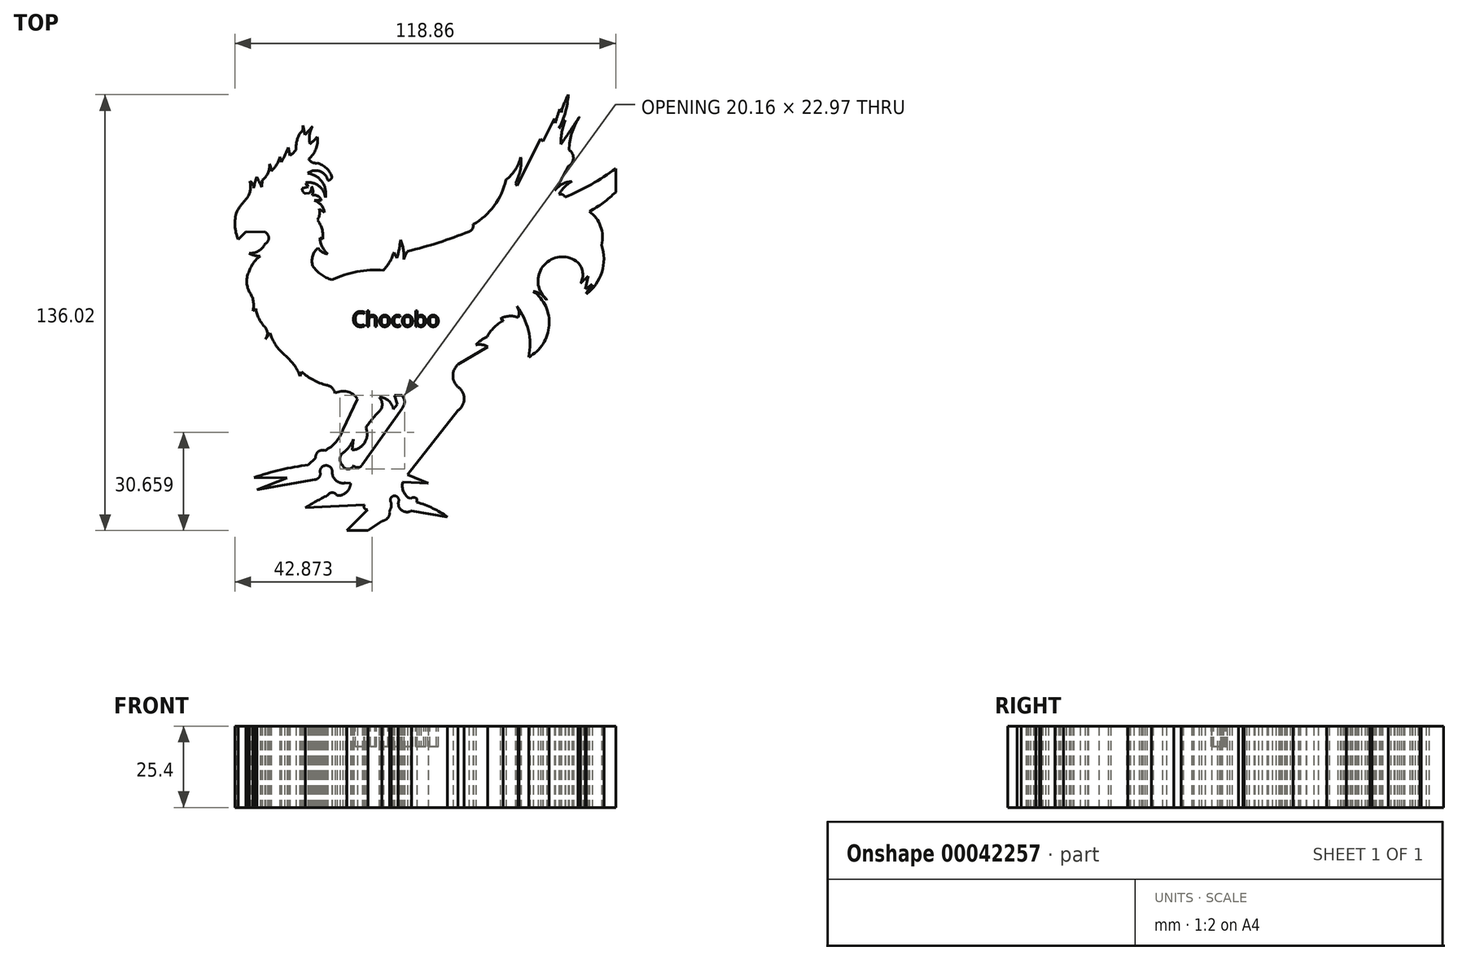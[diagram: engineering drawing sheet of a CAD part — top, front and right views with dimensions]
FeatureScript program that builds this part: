
annotation { "Feature Type Name" : "Feature", "Feature Type Description" : "" }
export const myFeature = defineFeature(function(context is Context, id is Id, definition is map)
    precondition{}
    {
        {
            var Q0;
            Q0=qCreatedBy(makeId("Top.planeOp"),FACE);
            var sketch = newSketch(context, id + "F0", { "sketchPlane" : qUnion([Q0])});
            skPoint(sketch, "E0", {"position": v(0, 127) * mm});
            skPoint(sketch, "E1", {"position": v(43.07, 0) * mm});
            skPoint(sketch, "E2", {"position": v(49.64, 0) * mm});
            skPoint(sketch, "E3", {"position": v(74.47, 4.17) * mm});
            skPoint(sketch, "E4", {"position": v(30.16, 7.09) * mm});
            skPoint(sketch, "E5", {"position": v(53.96, 2.95) * mm});
            skArc(sketch, "E6", {"start": v(48.55, 7.99) * mm, "mid": v(48.58, 6.94) * mm, "end": v(49.55, 6.53) * mm});
            skLineSegment(sketch, "E7", {"start": v(49.55, 6.53) * mm, "end": v(43.07, 0) * mm});
            skLineSegment(sketch, "E8", {"start": v(43.07, 0) * mm, "end": v(49.64, 0) * mm});
            skLineSegment(sketch, "E9", {"start": v(49.64, 0) * mm, "end": v(53.96, 2.95) * mm});
            skLineSegment(sketch, "E10", {"start": v(30.16, 7.09) * mm, "end": v(48.55, 7.99) * mm});
            skPoint(sketch, "E11", {"position": v(37.05, 10.94) * mm});
            skArc(sketch, "E12", {"start": v(37.05, 10.94) * mm, "mid": v(33.53, 9.15) * mm, "end": v(30.16, 7.09) * mm});
            skArc(sketch, "E13", {"start": v(40, 10.94) * mm, "mid": v(38.52, 11.85) * mm, "end": v(37.05, 10.94) * mm});
            skArc(sketch, "E14", {"start": v(40, 10.94) * mm, "mid": v(42.95, 11.93) * mm, "end": v(44.25, 14.75) * mm});
            skArc(sketch, "E15", {"start": v(53.96, 2.95) * mm, "mid": v(55.9, 4.03) * mm, "end": v(56.46, 6.17) * mm});
            skArc(sketch, "E16", {"start": v(59.19, 8.98) * mm, "mid": v(57.8, 10.82) * mm, "end": v(56.93, 8.68) * mm});
            skArc(sketch, "E17", {"start": v(56.46, 6.17) * mm, "mid": v(56.91, 7.39) * mm, "end": v(56.93, 8.68) * mm});
            skArc(sketch, "E18", {"start": v(59.19, 8.98) * mm, "mid": v(60.32, 6.26) * mm, "end": v(63.26, 6.17) * mm});
            skLineSegment(sketch, "E19", {"start": v(63.26, 6.17) * mm, "end": v(74.47, 4.17) * mm});
            skPoint(sketch, "E20", {"position": v(64.97, 8.83) * mm});
            skPoint(sketch, "E21", {"position": v(64.97, 9.94) * mm});
            skPoint(sketch, "E22", {"position": v(62.86, 9.94) * mm});
            skArc(sketch, "E23", {"start": v(74.47, 4.17) * mm, "mid": v(69.94, 6.95) * mm, "end": v(64.97, 8.83) * mm});
            skLineSegment(sketch, "E24", {"start": v(64.97, 8.83) * mm, "end": v(64.97, 9.94) * mm});
            skArc(sketch, "E25", {"start": v(64.97, 9.94) * mm, "mid": v(63.91, 10.34) * mm, "end": v(62.86, 9.94) * mm});
            skArc(sketch, "E26", {"start": v(60.55, 15.16) * mm, "mid": v(60.78, 12.14) * mm, "end": v(62.86, 9.94) * mm});
            skArc(sketch, "E27", {"start": v(38.52, 18.21) * mm, "mid": v(36.65, 20.32) * mm, "end": v(34.7, 18.3) * mm});
            skArc(sketch, "E28", {"start": v(38.52, 18.21) * mm, "mid": v(39.76, 15.56) * mm, "end": v(42.61, 14.87) * mm});
            skLineSegment(sketch, "E29", {"start": v(42.61, 14.87) * mm, "end": v(44.25, 14.75) * mm});
            skPoint(sketch, "E30", {"position": v(33.07, 15.89) * mm});
            skPoint(sketch, "E31", {"position": v(24.37, 16.42) * mm});
            skPoint(sketch, "E32", {"position": v(14.07, 16.56) * mm});
            skPoint(sketch, "E33", {"position": v(15.04, 12.74) * mm});
            skPoint(sketch, "E34", {"position": v(31.04, 20.48) * mm});
            skArc(sketch, "E35", {"start": v(33.07, 15.89) * mm, "mid": v(34.49, 16.68) * mm, "end": v(34.7, 18.3) * mm});
            skLineSegment(sketch, "E36", {"start": v(15.04, 12.74) * mm, "end": v(33.07, 15.89) * mm});
            skLineSegment(sketch, "E37", {"start": v(24.37, 16.42) * mm, "end": v(15.04, 12.74) * mm});
            skLineSegment(sketch, "E38", {"start": v(24.37, 16.42) * mm, "end": v(14.07, 16.56) * mm});
            skArc(sketch, "E39", {"start": v(31.04, 20.48) * mm, "mid": v(22.46, 18.95) * mm, "end": v(14.07, 16.56) * mm});
            skPoint(sketch, "E40", {"position": v(68.53, 14.79) * mm});
            skPoint(sketch, "E41", {"position": v(61.96, 17.38) * mm});
            skLineSegment(sketch, "E42", {"start": v(60.55, 15.16) * mm, "end": v(68.53, 14.79) * mm});
            skLineSegment(sketch, "E43", {"start": v(61.96, 17.38) * mm, "end": v(68.53, 14.79) * mm});
            skPoint(sketch, "E44", {"position": v(77.8, 37.53) * mm});
            skPoint(sketch, "E45", {"position": v(77.8, 44.79) * mm});
            skPoint(sketch, "E46", {"position": v(77.8, 51.83) * mm});
            skPoint(sketch, "E47", {"position": v(87.07, 57.37) * mm});
            skLineSegment(sketch, "E48", {"start": v(61.96, 17.38) * mm, "end": v(77.8, 37.53) * mm});
            skArc(sketch, "E49", {"start": v(77.8, 37.53) * mm, "mid": v(79.7, 41.16) * mm, "end": v(77.8, 44.79) * mm});
            skArc(sketch, "E50", {"start": v(77.8, 51.83) * mm, "mid": v(76.19, 48.3) * mm, "end": v(77.8, 44.79) * mm});
            skLineSegment(sketch, "E51", {"start": v(77.8, 51.83) * mm, "end": v(87.07, 57.37) * mm});
            skPoint(sketch, "E52", {"position": v(57.6, 37.83) * mm});
            skPoint(sketch, "E53", {"position": v(58.8, 39.39) * mm});
            skPoint(sketch, "E54", {"position": v(57.94, 42.15) * mm});
            skPoint(sketch, "E55", {"position": v(60.36, 42.15) * mm});
            skPoint(sketch, "E56", {"position": v(60.36, 38.18) * mm});
            skPoint(sketch, "E57", {"position": v(47.86, 20.6) * mm});
            skPoint(sketch, "E58", {"position": v(45.19, 20.33) * mm});
            skLineSegment(sketch, "E59", {"start": v(58.8, 39.39) * mm, "end": v(57.6, 37.83) * mm});
            skLineSegment(sketch, "E60", {"start": v(57.94, 42.15) * mm, "end": v(58.8, 39.39) * mm});
            skLineSegment(sketch, "E61", {"start": v(57.94, 42.15) * mm, "end": v(60.36, 42.15) * mm});
            skArc(sketch, "E62", {"start": v(60.36, 38.18) * mm, "mid": v(61.1, 40.16) * mm, "end": v(60.36, 42.15) * mm});
            skArc(sketch, "E63", {"start": v(57.6, 37.83) * mm, "mid": v(56.09, 40.52) * mm, "end": v(53.2, 41.61) * mm});
            skArc(sketch, "E64", {"start": v(45.19, 20.33) * mm, "mid": v(46.6, 19.67) * mm, "end": v(47.86, 20.6) * mm});
            skArc(sketch, "E65", {"start": v(41.76, 20.33) * mm, "mid": v(43.47, 19.17) * mm, "end": v(45.19, 20.33) * mm});
            skArc(sketch, "E66", {"start": v(41.76, 24.18) * mm, "mid": v(40.93, 22.25) * mm, "end": v(41.76, 20.33) * mm});
            skPoint(sketch, "E67", {"position": v(45.08, 28.47) * mm});
            skPoint(sketch, "E68", {"position": v(44.8, 25.13) * mm});
            skPoint(sketch, "E69", {"position": v(49.03, 32.1) * mm});
            skPoint(sketch, "E70", {"position": v(53.35, 38.93) * mm});
            skArc(sketch, "E71", {"start": v(41.76, 24.18) * mm, "mid": v(43.76, 26.06) * mm, "end": v(45.08, 28.47) * mm});
            skLineSegment(sketch, "E72", {"start": v(45.08, 28.47) * mm, "end": v(44.8, 25.13) * mm});
            skArc(sketch, "E73", {"start": v(44.8, 25.13) * mm, "mid": v(48.7, 27.53) * mm, "end": v(49.03, 32.1) * mm});
            skArc(sketch, "E74", {"start": v(53.14, 37.1) * mm, "mid": v(50.92, 34.73) * mm, "end": v(49.03, 32.1) * mm});
            skArc(sketch, "E75", {"start": v(53.14, 37.1) * mm, "mid": v(54.1, 39.34) * mm, "end": v(53.2, 41.61) * mm});
            skArc(sketch, "E76", {"start": v(36.2, 24.96) * mm, "mid": v(34.11, 24.6) * mm, "end": v(33.35, 22.6) * mm});
            skLineSegment(sketch, "E77", {"start": v(33.35, 22.6) * mm, "end": v(31.04, 20.48) * mm});
            skPoint(sketch, "E78", {"position": v(41.87, 31.4) * mm});
            skArc(sketch, "E79", {"start": v(36.2, 24.96) * mm, "mid": v(39.67, 27.62) * mm, "end": v(41.87, 31.4) * mm});
            skPoint(sketch, "E80", {"position": v(46.33, 41.08) * mm});
            skLineSegment(sketch, "E81", {"start": v(41.87, 31.4) * mm, "end": v(46.33, 41.08) * mm});
            skLineSegment(sketch, "E82", {"start": v(60.36, 38.18) * mm, "end": v(47.86, 20.6) * mm});
            skPoint(sketch, "E83", {"position": v(39.37, 42.82) * mm});
            skPoint(sketch, "E84", {"position": v(29.02, 49.53) * mm});
            skPoint(sketch, "E85", {"position": v(28.49, 48.23) * mm});
            skPoint(sketch, "E86", {"position": v(19.13, 61.65) * mm});
            skPoint(sketch, "E87", {"position": v(17.72, 59.72) * mm});
            skPoint(sketch, "E88", {"position": v(17.38, 63.64) * mm});
            skPoint(sketch, "E89", {"position": v(12.6, 80.95) * mm});
            skArc(sketch, "E90", {"start": v(46.33, 41.08) * mm, "mid": v(43.2, 43.35) * mm, "end": v(39.37, 42.82) * mm});
            skArc(sketch, "E91", {"start": v(29.02, 49.53) * mm, "mid": v(32.63, 46.97) * mm, "end": v(36.75, 45.38) * mm});
            skArc(sketch, "E92", {"start": v(39.37, 42.82) * mm, "mid": v(38.47, 44.52) * mm, "end": v(36.75, 45.38) * mm});
            skLineSegment(sketch, "E93", {"start": v(29.02, 49.53) * mm, "end": v(28.49, 48.23) * mm});
            skPoint(sketch, "E94", {"position": v(23.61, 54.8) * mm});
            skArc(sketch, "E95", {"start": v(28.49, 48.23) * mm, "mid": v(26.48, 51.83) * mm, "end": v(23.61, 54.8) * mm});
            skArc(sketch, "E96", {"start": v(19.13, 61.65) * mm, "mid": v(20.87, 57.9) * mm, "end": v(23.61, 54.8) * mm});
            skLineSegment(sketch, "E97", {"start": v(19.13, 61.65) * mm, "end": v(17.72, 59.72) * mm});
            skArc(sketch, "E98", {"start": v(17.72, 59.72) * mm, "mid": v(18.28, 61.75) * mm, "end": v(17.38, 63.64) * mm});
            skArc(sketch, "E99", {"start": v(14.67, 69.24) * mm, "mid": v(15.6, 66.24) * mm, "end": v(17.38, 63.64) * mm});
            skPoint(sketch, "E100", {"position": v(13.75, 68.48) * mm});
            skLineSegment(sketch, "E101", {"start": v(14.67, 69.24) * mm, "end": v(13.75, 68.48) * mm});
            skPoint(sketch, "E102", {"position": v(12.65, 74.5) * mm});
            skArc(sketch, "E103", {"start": v(13.75, 68.48) * mm, "mid": v(13.88, 71.61) * mm, "end": v(12.65, 74.5) * mm});
            skArc(sketch, "E104", {"start": v(12.6, 80.95) * mm, "mid": v(11.84, 77.72) * mm, "end": v(12.65, 74.5) * mm});
            skArc(sketch, "E105", {"start": v(16.04, 85.65) * mm, "mid": v(13.96, 83.57) * mm, "end": v(12.6, 80.95) * mm});
            skPoint(sketch, "E106", {"position": v(12.6, 86.54) * mm});
            skPoint(sketch, "E107", {"position": v(9.2, 90.83) * mm});
            skPoint(sketch, "E108", {"position": v(11.6, 93.24) * mm});
            skPoint(sketch, "E109", {"position": v(17.5, 93.15) * mm});
            skPoint(sketch, "E110", {"position": v(17.5, 89.47) * mm});
            skArc(sketch, "E111", {"start": v(12.6, 86.54) * mm, "mid": v(14.26, 85.83) * mm, "end": v(16.04, 85.65) * mm});
            skArc(sketch, "E112", {"start": v(12.6, 86.54) * mm, "mid": v(15.51, 87.25) * mm, "end": v(17.5, 89.47) * mm});
            skArc(sketch, "E113", {"start": v(17.5, 89.47) * mm, "mid": v(18.7, 91.31) * mm, "end": v(17.5, 93.15) * mm});
            skLineSegment(sketch, "E114", {"start": v(11.6, 93.24) * mm, "end": v(9.2, 90.83) * mm});
            skLineSegment(sketch, "E115", {"start": v(11.6, 93.24) * mm, "end": v(17.5, 93.15) * mm});
            skArc(sketch, "E116", {"start": v(8.74, 99.54) * mm, "mid": v(8.16, 95.15) * mm, "end": v(9.2, 90.83) * mm});
            skArc(sketch, "E117", {"start": v(11.99, 103.82) * mm, "mid": v(10.23, 101.78) * mm, "end": v(8.74, 99.54) * mm});
            skPoint(sketch, "E118", {"position": v(12.8, 109.01) * mm});
            skPoint(sketch, "E119", {"position": v(14.97, 110.35) * mm});
            skPoint(sketch, "E120", {"position": v(16.57, 107.21) * mm});
            skPoint(sketch, "E121", {"position": v(14, 106.85) * mm});
            skArc(sketch, "E122", {"start": v(11.99, 103.82) * mm, "mid": v(12.96, 106.32) * mm, "end": v(12.8, 109.01) * mm});
            skArc(sketch, "E123", {"start": v(14, 106.85) * mm, "mid": v(13.72, 108.1) * mm, "end": v(12.8, 109.01) * mm});
            skArc(sketch, "E124", {"start": v(14.97, 110.35) * mm, "mid": v(14.43, 108.62) * mm, "end": v(14, 106.85) * mm});
            skArc(sketch, "E125", {"start": v(14.97, 110.35) * mm, "mid": v(15.74, 108.77) * mm, "end": v(16.57, 107.21) * mm});
            skPoint(sketch, "E126", {"position": v(16.62, 109.32) * mm});
            skPoint(sketch, "E127", {"position": v(18.98, 114.31) * mm});
            skArc(sketch, "E128", {"start": v(16.62, 109.32) * mm, "mid": v(18.45, 111.51) * mm, "end": v(18.98, 114.31) * mm});
            skLineSegment(sketch, "E129", {"start": v(16.62, 109.32) * mm, "end": v(16.57, 107.21) * mm});
            skPoint(sketch, "E130", {"position": v(19.45, 112.15) * mm});
            skPoint(sketch, "E131", {"position": v(22.64, 114.93) * mm});
            skPoint(sketch, "E132", {"position": v(22.17, 116.58) * mm});
            skPoint(sketch, "E133", {"position": v(24.85, 119.51) * mm});
            skPoint(sketch, "E134", {"position": v(25.26, 117.04) * mm});
            skPoint(sketch, "E135", {"position": v(27.27, 118.95) * mm});
            skPoint(sketch, "E136", {"position": v(28.35, 123.89) * mm});
            skPoint(sketch, "E137", {"position": v(29.38, 126.4) * mm});
            skPoint(sketch, "E138", {"position": v(30.05, 123.42) * mm});
            skPoint(sketch, "E139", {"position": v(32.36, 126.1) * mm});
            skPoint(sketch, "E140", {"position": v(33.85, 122.86) * mm});
            skPoint(sketch, "E141", {"position": v(31.13, 115.96) * mm});
            skPoint(sketch, "E142", {"position": v(38.38, 110.36) * mm});
            skPoint(sketch, "E143", {"position": v(37.15, 109.27) * mm});
            skPoint(sketch, "E144", {"position": v(30.87, 111.49) * mm});
            skPoint(sketch, "E145", {"position": v(36.38, 103.92) * mm});
            skPoint(sketch, "E146", {"position": v(30.3, 108.55) * mm});
            skPoint(sketch, "E147", {"position": v(31.02, 107.27) * mm});
            skPoint(sketch, "E148", {"position": v(29.22, 106.8) * mm});
            skPoint(sketch, "E149", {"position": v(31.28, 105.26) * mm});
            skPoint(sketch, "E150", {"position": v(32.1, 107.37) * mm});
            skPoint(sketch, "E151", {"position": v(32.26, 104.7) * mm});
            skPoint(sketch, "E152", {"position": v(35.14, 103.05) * mm});
            skPoint(sketch, "E153", {"position": v(32.93, 103) * mm});
            skPoint(sketch, "E154", {"position": v(36.07, 99.24) * mm});
            skPoint(sketch, "E155", {"position": v(34.42, 100.37) * mm});
            skPoint(sketch, "E156", {"position": v(33.9, 96.92) * mm});
            skLineSegment(sketch, "E157", {"start": v(22.17, 116.58) * mm, "end": v(22.64, 114.93) * mm});
            skLineSegment(sketch, "E158", {"start": v(24.85, 119.51) * mm, "end": v(25.26, 117.04) * mm});
            skLineSegment(sketch, "E159", {"start": v(29.38, 126.4) * mm, "end": v(30.05, 123.42) * mm});
            skArc(sketch, "E160", {"start": v(19.45, 112.15) * mm, "mid": v(19.36, 113.26) * mm, "end": v(18.98, 114.31) * mm});
            skArc(sketch, "E161", {"start": v(19.45, 112.15) * mm, "mid": v(21.17, 114.15) * mm, "end": v(22.17, 116.58) * mm});
            skArc(sketch, "E162", {"start": v(22.64, 114.93) * mm, "mid": v(23.78, 117.2) * mm, "end": v(24.85, 119.51) * mm});
            skArc(sketch, "E163", {"start": v(25.26, 117.04) * mm, "mid": v(26.4, 117.85) * mm, "end": v(27.27, 118.95) * mm});
            skArc(sketch, "E164", {"start": v(28.35, 123.89) * mm, "mid": v(27.47, 121.5) * mm, "end": v(27.27, 118.95) * mm});
            skArc(sketch, "E165", {"start": v(28.35, 123.89) * mm, "mid": v(29.26, 124.99) * mm, "end": v(29.38, 126.4) * mm});
            skLineSegment(sketch, "E166", {"start": v(30.05, 123.42) * mm, "end": v(32.36, 126.1) * mm});
            skArc(sketch, "E167", {"start": v(32.36, 126.1) * mm, "mid": v(31.45, 123.5) * mm, "end": v(31.58, 120.75) * mm});
            skArc(sketch, "E168", {"start": v(31.58, 120.75) * mm, "mid": v(32.8, 121.72) * mm, "end": v(33.85, 122.86) * mm});
            skArc(sketch, "E169", {"start": v(31.13, 115.96) * mm, "mid": v(33.44, 119.03) * mm, "end": v(33.85, 122.86) * mm});
            skArc(sketch, "E170", {"start": v(38.38, 110.36) * mm, "mid": v(36.68, 113.1) * mm, "end": v(33.86, 114.66) * mm});
            skArc(sketch, "E171", {"start": v(31.13, 115.96) * mm, "mid": v(32.3, 114.91) * mm, "end": v(33.86, 114.66) * mm});
            skArc(sketch, "E172", {"start": v(37.15, 109.27) * mm, "mid": v(38, 109.55) * mm, "end": v(38.38, 110.36) * mm});
            skArc(sketch, "E173", {"start": v(37.15, 109.27) * mm, "mid": v(34.63, 112.13) * mm, "end": v(30.87, 111.49) * mm});
            skArc(sketch, "E174", {"start": v(36.38, 103.92) * mm, "mid": v(35.29, 108.92) * mm, "end": v(30.87, 111.49) * mm});
            skArc(sketch, "E175", {"start": v(36.38, 103.92) * mm, "mid": v(34.33, 107.54) * mm, "end": v(30.3, 108.55) * mm});
            skLineSegment(sketch, "E176", {"start": v(30.3, 108.55) * mm, "end": v(31.02, 107.27) * mm});
            skLineSegment(sketch, "E177", {"start": v(31.02, 107.27) * mm, "end": v(29.22, 106.8) * mm});
            skArc(sketch, "E178", {"start": v(29.22, 106.8) * mm, "mid": v(29.36, 105.8) * mm, "end": v(30.16, 105.19) * mm});
            skArc(sketch, "E179", {"start": v(31.28, 105.26) * mm, "mid": v(31.93, 106.22) * mm, "end": v(32.1, 107.37) * mm});
            skLineSegment(sketch, "E180", {"start": v(30.16, 105.19) * mm, "end": v(31.28, 105.26) * mm});
            skArc(sketch, "E181", {"start": v(32.26, 104.7) * mm, "mid": v(32.52, 106.05) * mm, "end": v(32.1, 107.37) * mm});
            skArc(sketch, "E182", {"start": v(35.14, 103.05) * mm, "mid": v(33.98, 104.37) * mm, "end": v(32.26, 104.7) * mm});
            skLineSegment(sketch, "E183", {"start": v(32.93, 103) * mm, "end": v(35.14, 103.05) * mm});
            skArc(sketch, "E184", {"start": v(36.07, 99.24) * mm, "mid": v(35.06, 101.6) * mm, "end": v(32.93, 103) * mm});
            skLineSegment(sketch, "E185", {"start": v(34.42, 100.37) * mm, "end": v(36.07, 99.24) * mm});
            skArc(sketch, "E186", {"start": v(33.9, 96.92) * mm, "mid": v(34.55, 98.6) * mm, "end": v(34.42, 100.37) * mm});
            skArc(sketch, "E187", {"start": v(35.57, 90.92) * mm, "mid": v(35.34, 94.09) * mm, "end": v(33.9, 96.92) * mm});
            skPoint(sketch, "E188", {"position": v(34.68, 91.32) * mm});
            skPoint(sketch, "E189", {"position": v(37.16, 86.31) * mm});
            skArc(sketch, "E190", {"start": v(34.68, 91.32) * mm, "mid": v(35.4, 88.55) * mm, "end": v(37.16, 86.31) * mm});
            skLineSegment(sketch, "E191", {"start": v(34.68, 91.32) * mm, "end": v(35.57, 90.92) * mm});
            skPoint(sketch, "E192", {"position": v(34.13, 88.22) * mm});
            skPoint(sketch, "E193", {"position": v(32.47, 82.6) * mm});
            skArc(sketch, "E194", {"start": v(34.13, 88.22) * mm, "mid": v(35.4, 86.88) * mm, "end": v(37.16, 86.31) * mm});
            skArc(sketch, "E195", {"start": v(34.13, 88.22) * mm, "mid": v(32.42, 85.67) * mm, "end": v(32.47, 82.6) * mm});
            skArc(sketch, "E196", {"start": v(32.47, 82.6) * mm, "mid": v(35.04, 79.88) * mm, "end": v(38.41, 78.27) * mm});
            skArc(sketch, "E197", {"start": v(54.53, 81.24) * mm, "mid": v(46.28, 80.77) * mm, "end": v(38.41, 78.27) * mm});
            skPoint(sketch, "E198", {"position": v(57.77, 86.73) * mm});
            skPoint(sketch, "E199", {"position": v(58.76, 85.16) * mm});
            skPoint(sketch, "E200", {"position": v(59.84, 90.7) * mm});
            skPoint(sketch, "E201", {"position": v(60.86, 84.6) * mm});
            skPoint(sketch, "E202", {"position": v(61.97, 87.1) * mm});
            skPoint(sketch, "E203", {"position": v(81.24, 93.29) * mm});
            skPoint(sketch, "E204", {"position": v(82.48, 95.51) * mm});
            skArc(sketch, "E205", {"start": v(58.76, 85.16) * mm, "mid": v(59.42, 87.9) * mm, "end": v(59.84, 90.7) * mm});
            skArc(sketch, "E206", {"start": v(54.53, 81.24) * mm, "mid": v(56.43, 83.82) * mm, "end": v(57.77, 86.73) * mm});
            skArc(sketch, "E207", {"start": v(61.97, 87.1) * mm, "mid": v(61.34, 85.89) * mm, "end": v(60.86, 84.6) * mm});
            skArc(sketch, "E208", {"start": v(81.24, 93.29) * mm, "mid": v(82.3, 94.16) * mm, "end": v(82.48, 95.51) * mm});
            skLineSegment(sketch, "E209", {"start": v(57.77, 86.73) * mm, "end": v(58.76, 84.94) * mm});
            skLineSegment(sketch, "E210", {"start": v(58.76, 84.94) * mm, "end": v(58.76, 85.16) * mm});
            skArc(sketch, "E211", {"start": v(60.86, 84.6) * mm, "mid": v(60.74, 87.71) * mm, "end": v(59.84, 90.7) * mm});
            skArc(sketch, "E212", {"start": v(61.97, 87.1) * mm, "mid": v(71.71, 89.87) * mm, "end": v(81.24, 93.29) * mm});
            skArc(sketch, "E213", {"start": v(82.48, 95.51) * mm, "mid": v(89.09, 101.4) * mm, "end": v(92.76, 109.46) * mm});
            skArc(sketch, "E214", {"start": v(92.76, 109.46) * mm, "mid": v(95.64, 112.6) * mm, "end": v(97.33, 116.49) * mm});
            skArc(sketch, "E215", {"start": v(95.62, 108.34) * mm, "mid": v(97.17, 112.27) * mm, "end": v(97.33, 116.49) * mm});
            skPoint(sketch, "E216", {"position": v(96.17, 107.64) * mm});
            skLineSegment(sketch, "E217", {"start": v(95.62, 108.34) * mm, "end": v(96.17, 107.64) * mm});
            skPoint(sketch, "E218", {"position": v(103.58, 122.2) * mm});
            skPoint(sketch, "E219", {"position": v(104.24, 121.5) * mm});
            skPoint(sketch, "E220", {"position": v(107.87, 128.54) * mm});
            skPoint(sketch, "E221", {"position": v(108.14, 127.14) * mm});
            skPoint(sketch, "E222", {"position": v(109.54, 131.46) * mm});
            skPoint(sketch, "E223", {"position": v(110, 130.52) * mm});
            skPoint(sketch, "E224", {"position": v(112.18, 136.02) * mm});
            skPoint(sketch, "E225", {"position": v(109.3, 125.47) * mm});
            skPoint(sketch, "E226", {"position": v(111.28, 128.05) * mm});
            skPoint(sketch, "E227", {"position": v(109.89, 120.56) * mm});
            skPoint(sketch, "E228", {"position": v(115.67, 129.1) * mm});
            skPoint(sketch, "E229", {"position": v(112.43, 118.82) * mm});
            skLineSegment(sketch, "E230", {"start": v(103.58, 122.2) * mm, "end": v(96.17, 107.64) * mm});
            skLineSegment(sketch, "E231", {"start": v(103.58, 122.2) * mm, "end": v(104.24, 121.5) * mm});
            skLineSegment(sketch, "E232", {"start": v(107.87, 128.54) * mm, "end": v(104.24, 121.5) * mm});
            skLineSegment(sketch, "E233", {"start": v(107.87, 128.54) * mm, "end": v(108.14, 127.14) * mm});
            skArc(sketch, "E234", {"start": v(109.54, 131.46) * mm, "mid": v(108.78, 129.32) * mm, "end": v(108.14, 127.14) * mm});
            skArc(sketch, "E235", {"start": v(110, 130.52) * mm, "mid": v(109.85, 131.03) * mm, "end": v(109.54, 131.46) * mm});
            skArc(sketch, "E236", {"start": v(112.18, 136.02) * mm, "mid": v(110.95, 133.33) * mm, "end": v(110, 130.52) * mm});
            skArc(sketch, "E237", {"start": v(109.3, 125.47) * mm, "mid": v(111.3, 130.6) * mm, "end": v(112.18, 136.02) * mm});
            skLineSegment(sketch, "E238", {"start": v(111.28, 128.05) * mm, "end": v(109.3, 125.47) * mm});
            skArc(sketch, "E239", {"start": v(111.28, 128.05) * mm, "mid": v(110.18, 124.38) * mm, "end": v(109.89, 120.56) * mm});
            skArc(sketch, "E240", {"start": v(109.89, 120.56) * mm, "mid": v(112.84, 124.79) * mm, "end": v(115.67, 129.1) * mm});
            skArc(sketch, "E241", {"start": v(115.67, 129.1) * mm, "mid": v(113.33, 124.18) * mm, "end": v(112.43, 118.82) * mm});
            skArc(sketch, "E242", {"start": v(112.14, 113.68) * mm, "mid": v(113.77, 116.17) * mm, "end": v(112.43, 118.82) * mm});
            skArc(sketch, "E243", {"start": v(108, 106.14) * mm, "mid": v(110.13, 109.88) * mm, "end": v(112.14, 113.68) * mm});
            skArc(sketch, "E244", {"start": v(113.28, 108.96) * mm, "mid": v(110.34, 108.12) * mm, "end": v(108, 106.14) * mm});
            skArc(sketch, "E245", {"start": v(113.28, 108.96) * mm, "mid": v(111, 107.2) * mm, "end": v(109.29, 104.9) * mm});
            skArc(sketch, "E246", {"start": v(111.18, 104.02) * mm, "mid": v(110.4, 104.84) * mm, "end": v(109.29, 104.9) * mm});
            skArc(sketch, "E247", {"start": v(111.18, 104.02) * mm, "mid": v(119.35, 108.03) * mm, "end": v(127, 112.98) * mm});
            skArc(sketch, "E248", {"start": v(118.76, 99.59) * mm, "mid": v(123.1, 102.3) * mm, "end": v(127, 105.64) * mm});
            skLineSegment(sketch, "E249", {"start": v(127, 112.98) * mm, "end": v(127, 105.64) * mm});
            skPoint(sketch, "E250", {"position": v(122.57, 89.1) * mm});
            skPoint(sketch, "E251", {"position": v(117.75, 73.81) * mm});
            skPoint(sketch, "E252", {"position": v(119.7, 76.89) * mm});
            skPoint(sketch, "E253", {"position": v(117.54, 75.35) * mm});
            skPoint(sketch, "E254", {"position": v(118.45, 79.4) * mm});
            skPoint(sketch, "E255", {"position": v(116, 77.17) * mm});
            skPoint(sketch, "E256", {"position": v(115.17, 83.66) * mm});
            skPoint(sketch, "E257", {"position": v(105.48, 71.98) * mm});
            skPoint(sketch, "E258", {"position": v(101.3, 74.63) * mm});
            skPoint(sketch, "E259", {"position": v(99.83, 54.17) * mm});
            skArc(sketch, "E260", {"start": v(122.57, 89.1) * mm, "mid": v(122.27, 94.93) * mm, "end": v(118.76, 99.59) * mm});
            skArc(sketch, "E261", {"start": v(117.75, 73.81) * mm, "mid": v(122.67, 80.67) * mm, "end": v(122.57, 89.1) * mm});
            skLineSegment(sketch, "E262", {"start": v(116, 77.17) * mm, "end": v(118.45, 79.4) * mm});
            skLineSegment(sketch, "E263", {"start": v(117.54, 75.35) * mm, "end": v(118.45, 79.4) * mm});
            skLineSegment(sketch, "E264", {"start": v(119.7, 76.89) * mm, "end": v(117.75, 73.81) * mm});
            skLineSegment(sketch, "E265", {"start": v(117.54, 75.35) * mm, "end": v(119.7, 76.89) * mm});
            skArc(sketch, "E266", {"start": v(116, 77.17) * mm, "mid": v(116.68, 80.55) * mm, "end": v(115.17, 83.66) * mm});
            skArc(sketch, "E267", {"start": v(115.17, 83.66) * mm, "mid": v(104.48, 82.66) * mm, "end": v(105.48, 71.98) * mm});
            skArc(sketch, "E268", {"start": v(105.48, 71.98) * mm, "mid": v(103.67, 73.76) * mm, "end": v(101.3, 74.63) * mm});
            skArc(sketch, "E269", {"start": v(99.83, 54.17) * mm, "mid": v(106.23, 64) * mm, "end": v(101.3, 74.63) * mm});
            skArc(sketch, "E270", {"start": v(87.07, 57.37) * mm, "mid": v(85.27, 58) * mm, "end": v(83.35, 57.94) * mm});
            skArc(sketch, "E271", {"start": v(86.84, 60.52) * mm, "mid": v(84.99, 59.38) * mm, "end": v(83.35, 57.94) * mm});
            skArc(sketch, "E272", {"start": v(91.8, 65.48) * mm, "mid": v(88.98, 63.34) * mm, "end": v(86.84, 60.52) * mm});
            skPoint(sketch, "E273", {"position": v(91, 66.05) * mm});
            skArc(sketch, "E274", {"start": v(91.8, 65.48) * mm, "mid": v(91.53, 65.94) * mm, "end": v(91, 66.05) * mm});
            skArc(sketch, "E275", {"start": v(96.5, 66.42) * mm, "mid": v(93.7, 66.93) * mm, "end": v(91, 66.05) * mm});
            skArc(sketch, "E276", {"start": v(96.5, 66.42) * mm, "mid": v(96.8, 68.25) * mm, "end": v(96.13, 69.98) * mm});
            skArc(sketch, "E277", {"start": v(99.83, 54.17) * mm, "mid": v(99.72, 62.48) * mm, "end": v(96.13, 69.98) * mm});
            skSolve(sketch);
        }
        {
            var Q0;
            Q0 = qSketchRegion(id + "F0", true);
            extrude(context, id + "F1", {"entities" : qUnion([Q0]), "depth" : 25.4 * mm});
        }
        {
            var Q0;
            Q0=makeQuery(id+"F1.opExtrude","CAP_FACE",FACE,{"disambiguationData":[OSD([sQuery(id+"F0.wireOp",EDGE,"E6"),sQuery(id+"F0.wireOp",EDGE,"E7"),sQuery(id+"F0.wireOp",EDGE,"E8"),sQuery(id+"F0.wireOp",EDGE,"E9"),sQuery(id+"F0.wireOp",EDGE,"E10"),sQuery(id+"F0.wireOp",EDGE,"E12"),sQuery(id+"F0.wireOp",EDGE,"E13"),sQuery(id+"F0.wireOp",EDGE,"E14"),sQuery(id+"F0.wireOp",EDGE,"E15"),sQuery(id+"F0.wireOp",EDGE,"E16"),sQuery(id+"F0.wireOp",EDGE,"E17"),sQuery(id+"F0.wireOp",EDGE,"E18"),sQuery(id+"F0.wireOp",EDGE,"E19"),sQuery(id+"F0.wireOp",EDGE,"E23"),sQuery(id+"F0.wireOp",EDGE,"E24"),sQuery(id+"F0.wireOp",EDGE,"E25"),sQuery(id+"F0.wireOp",EDGE,"E26"),sQuery(id+"F0.wireOp",EDGE,"E27"),sQuery(id+"F0.wireOp",EDGE,"E28"),sQuery(id+"F0.wireOp",EDGE,"E29"),sQuery(id+"F0.wireOp",EDGE,"E35"),sQuery(id+"F0.wireOp",EDGE,"E36"),sQuery(id+"F0.wireOp",EDGE,"E37"),sQuery(id+"F0.wireOp",EDGE,"E38"),sQuery(id+"F0.wireOp",EDGE,"E39"),sQuery(id+"F0.wireOp",EDGE,"E42"),sQuery(id+"F0.wireOp",EDGE,"E43"),sQuery(id+"F0.wireOp",EDGE,"E48"),sQuery(id+"F0.wireOp",EDGE,"E49"),sQuery(id+"F0.wireOp",EDGE,"E50"),sQuery(id+"F0.wireOp",EDGE,"E51"),sQuery(id+"F0.wireOp",EDGE,"E59"),sQuery(id+"F0.wireOp",EDGE,"E60"),sQuery(id+"F0.wireOp",EDGE,"E61"),sQuery(id+"F0.wireOp",EDGE,"E62"),sQuery(id+"F0.wireOp",EDGE,"E63"),sQuery(id+"F0.wireOp",EDGE,"E64"),sQuery(id+"F0.wireOp",EDGE,"E65"),sQuery(id+"F0.wireOp",EDGE,"E66"),sQuery(id+"F0.wireOp",EDGE,"E71"),sQuery(id+"F0.wireOp",EDGE,"E72"),sQuery(id+"F0.wireOp",EDGE,"E73"),sQuery(id+"F0.wireOp",EDGE,"E74"),sQuery(id+"F0.wireOp",EDGE,"E75"),sQuery(id+"F0.wireOp",EDGE,"E76"),sQuery(id+"F0.wireOp",EDGE,"E77"),sQuery(id+"F0.wireOp",EDGE,"E79"),sQuery(id+"F0.wireOp",EDGE,"E81"),sQuery(id+"F0.wireOp",EDGE,"E82"),sQuery(id+"F0.wireOp",EDGE,"E90"),sQuery(id+"F0.wireOp",EDGE,"E91"),sQuery(id+"F0.wireOp",EDGE,"E92"),sQuery(id+"F0.wireOp",EDGE,"E93"),sQuery(id+"F0.wireOp",EDGE,"E95"),sQuery(id+"F0.wireOp",EDGE,"E96"),sQuery(id+"F0.wireOp",EDGE,"E97"),sQuery(id+"F0.wireOp",EDGE,"E98"),sQuery(id+"F0.wireOp",EDGE,"E99"),sQuery(id+"F0.wireOp",EDGE,"E101"),sQuery(id+"F0.wireOp",EDGE,"E103"),sQuery(id+"F0.wireOp",EDGE,"E104"),sQuery(id+"F0.wireOp",EDGE,"E105"),sQuery(id+"F0.wireOp",EDGE,"E111"),sQuery(id+"F0.wireOp",EDGE,"E112"),sQuery(id+"F0.wireOp",EDGE,"E113"),sQuery(id+"F0.wireOp",EDGE,"E114"),sQuery(id+"F0.wireOp",EDGE,"E115"),sQuery(id+"F0.wireOp",EDGE,"E116"),sQuery(id+"F0.wireOp",EDGE,"E117"),sQuery(id+"F0.wireOp",EDGE,"E122"),sQuery(id+"F0.wireOp",EDGE,"E123"),sQuery(id+"F0.wireOp",EDGE,"E124"),sQuery(id+"F0.wireOp",EDGE,"E125"),sQuery(id+"F0.wireOp",EDGE,"E128"),sQuery(id+"F0.wireOp",EDGE,"E129"),sQuery(id+"F0.wireOp",EDGE,"E157"),sQuery(id+"F0.wireOp",EDGE,"E158"),sQuery(id+"F0.wireOp",EDGE,"E159"),sQuery(id+"F0.wireOp",EDGE,"E160"),sQuery(id+"F0.wireOp",EDGE,"E161"),sQuery(id+"F0.wireOp",EDGE,"E162"),sQuery(id+"F0.wireOp",EDGE,"E163"),sQuery(id+"F0.wireOp",EDGE,"E164"),sQuery(id+"F0.wireOp",EDGE,"E165"),sQuery(id+"F0.wireOp",EDGE,"E166"),sQuery(id+"F0.wireOp",EDGE,"E167"),sQuery(id+"F0.wireOp",EDGE,"E168"),sQuery(id+"F0.wireOp",EDGE,"E169"),sQuery(id+"F0.wireOp",EDGE,"E170"),sQuery(id+"F0.wireOp",EDGE,"E171"),sQuery(id+"F0.wireOp",EDGE,"E172"),sQuery(id+"F0.wireOp",EDGE,"E173"),sQuery(id+"F0.wireOp",EDGE,"E174"),sQuery(id+"F0.wireOp",EDGE,"E175"),sQuery(id+"F0.wireOp",EDGE,"E176"),sQuery(id+"F0.wireOp",EDGE,"E177"),sQuery(id+"F0.wireOp",EDGE,"E178"),sQuery(id+"F0.wireOp",EDGE,"E179"),sQuery(id+"F0.wireOp",EDGE,"E180"),sQuery(id+"F0.wireOp",EDGE,"E181"),sQuery(id+"F0.wireOp",EDGE,"E182"),sQuery(id+"F0.wireOp",EDGE,"E183"),sQuery(id+"F0.wireOp",EDGE,"E184"),sQuery(id+"F0.wireOp",EDGE,"E185"),sQuery(id+"F0.wireOp",EDGE,"E186"),sQuery(id+"F0.wireOp",EDGE,"E187"),sQuery(id+"F0.wireOp",EDGE,"E190"),sQuery(id+"F0.wireOp",EDGE,"E191"),sQuery(id+"F0.wireOp",EDGE,"E194"),sQuery(id+"F0.wireOp",EDGE,"E195"),sQuery(id+"F0.wireOp",EDGE,"E196"),sQuery(id+"F0.wireOp",EDGE,"E197"),sQuery(id+"F0.wireOp",EDGE,"E205"),sQuery(id+"F0.wireOp",EDGE,"E206"),sQuery(id+"F0.wireOp",EDGE,"E207"),sQuery(id+"F0.wireOp",EDGE,"E208"),sQuery(id+"F0.wireOp",EDGE,"E209"),sQuery(id+"F0.wireOp",EDGE,"E210"),sQuery(id+"F0.wireOp",EDGE,"E211"),sQuery(id+"F0.wireOp",EDGE,"E212"),sQuery(id+"F0.wireOp",EDGE,"E213"),sQuery(id+"F0.wireOp",EDGE,"E214"),sQuery(id+"F0.wireOp",EDGE,"E215"),sQuery(id+"F0.wireOp",EDGE,"E217"),sQuery(id+"F0.wireOp",EDGE,"E230"),sQuery(id+"F0.wireOp",EDGE,"E231"),sQuery(id+"F0.wireOp",EDGE,"E232"),sQuery(id+"F0.wireOp",EDGE,"E233"),sQuery(id+"F0.wireOp",EDGE,"E234"),sQuery(id+"F0.wireOp",EDGE,"E235"),sQuery(id+"F0.wireOp",EDGE,"E236"),sQuery(id+"F0.wireOp",EDGE,"E237"),sQuery(id+"F0.wireOp",EDGE,"E238"),sQuery(id+"F0.wireOp",EDGE,"E239"),sQuery(id+"F0.wireOp",EDGE,"E240"),sQuery(id+"F0.wireOp",EDGE,"E241"),sQuery(id+"F0.wireOp",EDGE,"E242"),sQuery(id+"F0.wireOp",EDGE,"E243"),sQuery(id+"F0.wireOp",EDGE,"E244"),sQuery(id+"F0.wireOp",EDGE,"E245"),sQuery(id+"F0.wireOp",EDGE,"E246"),sQuery(id+"F0.wireOp",EDGE,"E247"),sQuery(id+"F0.wireOp",EDGE,"E248"),sQuery(id+"F0.wireOp",EDGE,"E249"),sQuery(id+"F0.wireOp",EDGE,"E260"),sQuery(id+"F0.wireOp",EDGE,"E261"),sQuery(id+"F0.wireOp",EDGE,"E262"),sQuery(id+"F0.wireOp",EDGE,"E263"),sQuery(id+"F0.wireOp",EDGE,"E264"),sQuery(id+"F0.wireOp",EDGE,"E265"),sQuery(id+"F0.wireOp",EDGE,"E266"),sQuery(id+"F0.wireOp",EDGE,"E267"),sQuery(id+"F0.wireOp",EDGE,"E268"),sQuery(id+"F0.wireOp",EDGE,"E269"),sQuery(id+"F0.wireOp",EDGE,"E270"),sQuery(id+"F0.wireOp",EDGE,"E271"),sQuery(id+"F0.wireOp",EDGE,"E272"),sQuery(id+"F0.wireOp",EDGE,"E274"),sQuery(id+"F0.wireOp",EDGE,"E275"),sQuery(id+"F0.wireOp",EDGE,"E276"),sQuery(id+"F0.wireOp",EDGE,"E277")])],"isStart":false});
            var sketch = newSketch(context, id + "F2", { "sketchPlane" : qUnion([Q0])});
            skText(sketch, "E278", { "text": "Chocobo", "fontName": "OpenSans-Regular.ttf"});
            const initialGuessF2  = {"E278": [0.04472, 0.06364, 1, 0, 0.00474]};
            skSetInitialGuess(sketch, initialGuessF2);
            skSolve(sketch);
        }
        {
            var Q0;
            Q0 = qSketchRegion(id + "F2", true);
            extrude(context, id + "F3", {"entities" : qUnion([Q0]), "operationType" : NewBodyOperationType.REMOVE, "oppositeDirection" : true, "depth" : 6.35 * mm});
        }
    });
